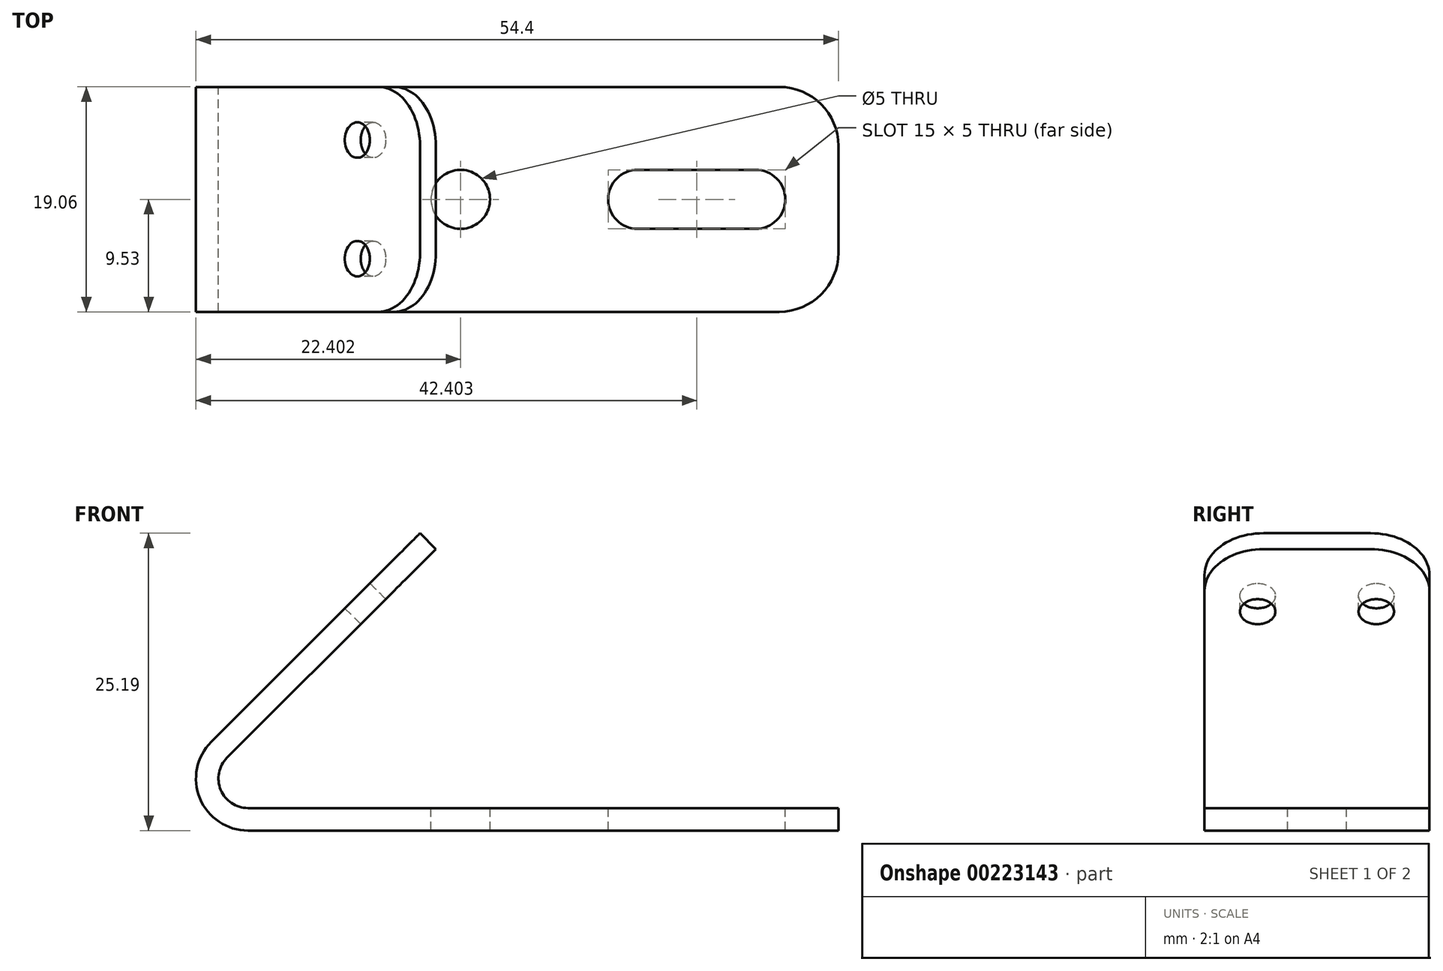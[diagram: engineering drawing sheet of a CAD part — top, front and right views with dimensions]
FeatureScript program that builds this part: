
annotation { "Feature Type Name" : "Feature", "Feature Type Description" : "" }
export const myFeature = defineFeature(function(context is Context, id is Id, definition is map)
    precondition{}
    {
        {
            var Q0;
            Q0=qCreatedBy(makeId("Front.planeOp"),FACE);
            var sketch = newSketch(context, id + "F0", { "sketchPlane" : qUnion([Q0])});
            skLineSegment(sketch, "E0", {"start": v(10.62, 0) * mm, "end": v(60.62, 0) * mm});
            skLineSegment(sketch, "E1", {"start": v(60.62, 0) * mm, "end": v(60.62, 1.9) * mm});
            skLineSegment(sketch, "E2", {"start": v(60.62, 1.9) * mm, "end": v(0, 1.9) * mm});
            skLineSegment(sketch, "E3", {"start": v(7.51, 7.51) * mm, "end": v(25.19, 25.19) * mm});
            skPoint(sketch, "E4.visualSharp", {"position": v(0, 0) * mm});
            skArc(sketch, "E4.filletArc", {"start": v(7.51, 7.51) * mm, "mid": v(6.56, 2.72) * mm, "end": v(10.62, 0) * mm});
            skLineSegment(sketch, "E5", {"start": v(25.19, 25.19) * mm, "end": v(26.53, 23.85) * mm});
            skLineSegment(sketch, "E6", {"start": v(26.53, 23.85) * mm, "end": v(8.85, 6.17) * mm});
            skArc(sketch, "E7", {"start": v(8.85, 6.17) * mm, "mid": v(8.31, 3.44) * mm, "end": v(10.62, 1.9) * mm});
            skSolve(sketch);
        }
        {
            var Q0;
            Q0 = qSketchRegion(id + "F0", true);
            extrude(context, id + "F1", {"entities" : qUnion([Q0]), "endBound" : BoundingType.SYMMETRIC, "depth" : 19.05 * mm});
        }
        {
            var Q0;
            Q0=makeQuery(id+"F1.opExtrude","SWEPT_FACE",FACE,{"disambiguationData":[OSD([sQuery(id+"F0.wireOp",EDGE,"E2")])]});
            var sketch = newSketch(context, id + "F2", { "sketchPlane" : qUnion([Q0])});
            skLineSegment(sketch, "E8.0", {"start": v(60.62, -9.53) * mm, "end": v(60.62, 9.52) * mm});
            skLineSegment(sketch, "E9.0", {"start": v(60.62, 9.53) * mm, "end": v(10.62, 9.53) * mm});
            skLineSegment(sketch, "E10.0", {"start": v(60.62, -9.53) * mm, "end": v(10.62, -9.53) * mm});
            skLineSegment(sketch, "E11", {"start": v(60.62, 0) * mm, "end": v(56.12, 0) * mm});
            skLineSegment(sketch, "E12", {"start": v(56.12, 0) * mm, "end": v(41.12, 0) * mm});
            skLineSegment(sketch, "E13", {"start": v(56.12, 0) * mm, "end": v(56.12, 2.5) * mm});
            skCircle(sketch, "E14", {"center": v(53.62, 0) * mm, "radius": 2.5 * mm});
            skCircle(sketch, "E15", {"center": v(43.62, 0) * mm, "radius": 2.5 * mm});
            skLineSegment(sketch, "E16", {"start": v(43.62, 2.5) * mm, "end": v(53.62, 2.5) * mm});
            skLineSegment(sketch, "E17", {"start": v(43.62, -2.5) * mm, "end": v(53.62, -2.5) * mm});
            skCircle(sketch, "E18", {"center": v(28.62, 0) * mm, "radius": 2.5 * mm});
            skSolve(sketch);
        }
        {
            var Q0;
            Q0 = qSketchRegion(id + "F2", true);
            extrude(context, id + "F3", {"entities" : qUnion([Q0]), "operationType" : NewBodyOperationType.REMOVE, "endBound" : BoundingType.THROUGH_ALL, "oppositeDirection" : true, "depth" : 25 * mm});
        }
        {
            var Q0;
            Q0=makeQuery(id+"F1.opExtrude","SWEPT_FACE",FACE,{"disambiguationData":[OSD([sQuery(id+"F0.wireOp",EDGE,"E3")])]});
            var sketch = newSketch(context, id + "F4", { "sketchPlane" : qUnion([Q0])});
            skLineSegment(sketch, "E19.0", {"start": v(9.53, 35.62) * mm, "end": v(-9.52, 35.62) * mm});
            skLineSegment(sketch, "E19.1", {"start": v(9.53, 10.62) * mm, "end": v(-9.52, 10.62) * mm});
            skLineSegment(sketch, "E19.2", {"start": v(-9.53, 10.62) * mm, "end": v(-9.53, 35.62) * mm});
            skLineSegment(sketch, "E19.3", {"start": v(9.53, 10.62) * mm, "end": v(9.53, 35.62) * mm});
            skLineSegment(sketch, "E20", {"start": v(-9.53, 35.62) * mm, "end": v(-9.53, 28.12) * mm});
            skCircle(sketch, "E21", {"center": v(-5.03, 28.12) * mm, "radius": 1.5 * mm});
            skLineSegment(sketch, "E22", {"start": v(9.53, 6.22) * mm, "end": v(-9.52, 6.22) * mm});
            skCircle(sketch, "E23", {"center": v(5.03, 28.12) * mm, "radius": 1.5 * mm});
            skSolve(sketch);
        }
        {
            var Q0;
            Q0=makeQuery(id+"F4.imprint","IMPRINT",FACE,{"disambiguationData":[TD([[makeQuery(id+"F4.imprint","IMPRINT",EDGE,{"derivedFrom":sQuery(id+"F4.wireOp",EDGE,"E21")}),1.0]])]});
            var Q1;
            Q1=makeQuery(id+"F4.imprint","IMPRINT",FACE,{"disambiguationData":[TD([[makeQuery(id+"F4.imprint","IMPRINT",EDGE,{"derivedFrom":sQuery(id+"F4.wireOp",EDGE,"E23")}),1.0]])]});
            extrude(context, id + "F5", {"entities" : qUnion([Q0, Q1]), "operationType" : NewBodyOperationType.REMOVE, "endBound" : BoundingType.UP_TO_NEXT, "oppositeDirection" : true, "depth" : 25 * mm});
        }
        {
            var Q0;
            Q0=makeQuery(id+"F1.opExtrude","CAP_EDGE",EDGE,{"disambiguationData":[OSD([sQuery(id+"F0.wireOp",EDGE,"E5")])],"isStart":true});
            var Q1;
            Q1=makeQuery(id+"F1.opExtrude","CAP_EDGE",EDGE,{"disambiguationData":[OSD([sQuery(id+"F0.wireOp",EDGE,"E5")])],"isStart":false});
            var Q2;
            Q2=makeQuery(id+"F1.opExtrude","CAP_EDGE",EDGE,{"disambiguationData":[OSD([sQuery(id+"F0.wireOp",EDGE,"E1")])],"isStart":false});
            var Q3;
            Q3=makeQuery(id+"F1.opExtrude","CAP_EDGE",EDGE,{"disambiguationData":[OSD([sQuery(id+"F0.wireOp",EDGE,"E1")])],"isStart":true});
            fillet(context, id + "F6", {"entities" : qUnion([Q0, Q1, Q2, Q3]), "radius" : 5 * mm, "tangentPropagation" : true, "allowEdgeOverflow" : false});
        }
    });
